# Revit family: QF_Vivreau_V3-202
name_source: partatom
category: Specialty Equipment
revit_build: Autodesk Revit 2018 (Build: 20190510_1515(x64)
units: mm (PartAtom-declared; Revit-internal decimal feet)

## family parameters
Always vertical = Yes
Cut with Voids When Loaded = No
OmniClass Number = 23.40.40.14.24
OmniClass Title = Food Dispensing Equipment
Part Type = Normal
Room Calculation Point = No
Round Connector Dimension = Use Diameter
Shared = No
Work Plane-Based = No

## types (1)
- QF_Vivreau_V3-202
    Apparent Power = 1320 VA
    Assembly Code = E1090320
    BTUH = 0.0 Btu/h
    CSI MasterFormat = 11 46 00
    Cold Water Connection Height = 2' - 0"
    Cold Water Flow = 1 GPM
    Cold Water Maximum Pressure = 90.00 psi
    Cold Water Minimum Pressure = 50.00 psi
    Cold Water RI Height = 0' - 0"
    Cold Water Size = 1"
    Cold Water Temperature Recommended = 60 °F
    Conn Conduit = No
    Conn Plug = 5-15P
    Cycle = 60 Hz
    Depth = 1' - 9 5/8"
    Description = Water Dispenser
    Elec Conn Connection Height = 2' - 0"
    Elec Conn RI Height = 0' - 0"
    Electric Connection Type = Plug
    FL Amps = 11 A
    Foodservice Equipment Identifier = Yes
    Identify Quantity as Lot = Yes
    Indirect Waste Connection Height = 1' - 4"
    Indirect Waste Connection Type = Vertical Stand Pipe
    Indirect Waste Flow = 0 GPM
    Indirect Waste Size = 1"
    Manufacturer = Vivreau
    Masterspec = Division 11
    Max Overcurrent Protection = 16 A
    Min Ckt Ampacity = 11 A
    Model = V3-202
    Number of Poles = 1
    Phase = 1
    Plumbing Connection Type = FNPT Ball Valve
    Plumbing Remarks = Cold Water Consumption Will Vary Based On Use, Indirect Waste Flow Willl Vary Based On Use
    Refrigerant Type = 134a
    Refrigerant Volume = 0.000288 kip
    Specification by Manufacturer = Vivreau High Volume Water Bottling System, dual tap, undercounter cabinet, self-contained ice bank refrigeration system, advanced micro-filtered, chilled still and sparkling water, twin tap with removable nozzles & stainless steel drip tray, accommodates up to 20 lb CO2 cylinder (cylinder not included), front feet, rear rollers, x1 20amp electrical receptacle (5-20 R) 120V 60Hz (11 amps), NEMA 5-20R, ETL, NSF (for indoor use only)
    URL = http://www.vivreauwater.com
    URL Cutsheet = https://www.vivreauwater.com
    Volts = 120 V
    Waste Water Discharge Temperature = 0 °F
    Watts = 1320 W
    Weight in Pounds = 195
    Width = 1' - 11 3/8"

## geometry (parser evidence)
native form markers: Sweep x15
no freeform markers — native parametric forms only
